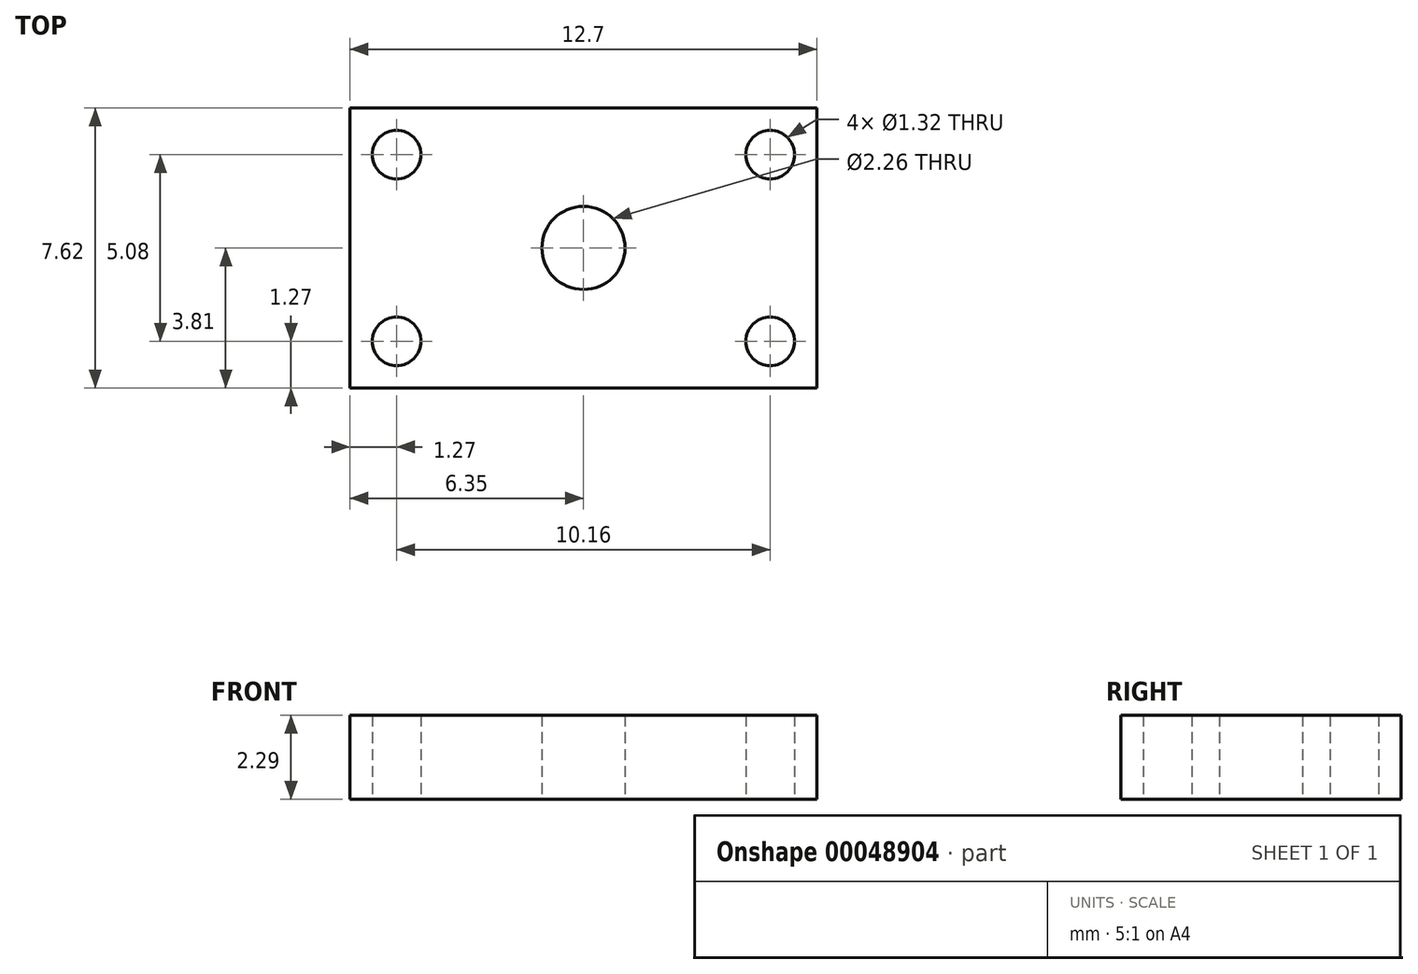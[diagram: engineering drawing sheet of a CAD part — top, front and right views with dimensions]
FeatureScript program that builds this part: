
annotation { "Feature Type Name" : "Feature", "Feature Type Description" : "" }
export const myFeature = defineFeature(function(context is Context, id is Id, definition is map)
    precondition{}
    {
        {
            var Q0;
            Q0=qCreatedBy(makeId("Top.planeOp"),FACE);
            var sketch = newSketch(context, id + "F0", { "sketchPlane" : qUnion([Q0])});
            skLineSegment(sketch, "E0.rect.bottom", {"start": v(-6.35, -3.8) * mm, "end": v(6.35, -3.8) * mm});
            skLineSegment(sketch, "E0.rect.top", {"start": v(-6.35, 3.8) * mm, "end": v(6.35, 3.8) * mm});
            skLineSegment(sketch, "E0.rect.left", {"start": v(-6.35, -3.8) * mm, "end": v(-6.35, 3.8) * mm});
            skLineSegment(sketch, "E0.rect.right", {"start": v(6.35, -3.8) * mm, "end": v(6.35, 3.8) * mm});
            skPoint(sketch, "E0.rect.middle", {"position": v(0, 0) * mm});
            skLineSegment(sketch, "E1.rect.bottom", {"start": v(-5.08, -2.54) * mm, "end": v(5.08, -2.54) * mm});
            skLineSegment(sketch, "E1.rect.top", {"start": v(-5.08, 2.54) * mm, "end": v(5.08, 2.54) * mm});
            skLineSegment(sketch, "E1.rect.left", {"start": v(-5.08, -2.54) * mm, "end": v(-5.08, 2.54) * mm});
            skLineSegment(sketch, "E1.rect.right", {"start": v(5.08, -2.54) * mm, "end": v(5.08, 2.54) * mm});
            skSolve(sketch);
        }
        {
            var Q0;
            Q0=makeQuery(id+"F0.imprint","IMPRINT",FACE,{"disambiguationData":[TD([[makeQuery(id+"F0.imprint","IMPRINT",EDGE,{"derivedFrom":sQuery(id+"F0.wireOp",EDGE,"E1.rect.bottom")}),1.0]])]});
            var Q1;
            Q1=makeQuery(id+"F0.imprint","IMPRINT",FACE,{"disambiguationData":[TD([[makeQuery(id+"F0.imprint","IMPRINT",EDGE,{"derivedFrom":sQuery(id+"F0.wireOp",EDGE,"E0.rect.bottom")}),1.0]])]});
            extrude(context, id + "F1", {"entities" : qUnion([Q0, Q1]), "depth" : 2.3 * mm});
        }
        {
            var Q0;
            Q0=sQuery(id+"F0.wireOp",VERTEX,"E1.rect.left.end");
            var Q1;
            Q1=sQuery(id+"F0.wireOp",VERTEX,"E1.rect.right.end");
            var Q2;
            Q2=sQuery(id+"F0.wireOp",VERTEX,"E1.rect.right.start");
            var Q3;
            Q3=sQuery(id+"F0.wireOp",VERTEX,"E1.rect.left.start");
            var Q4;
            Q4=makeQuery(id+"F1.opExtrude","SWEPT_BODY",BODY,{"disambiguationData":[OSD([sQuery(id+"F0.wireOp",EDGE,"E0.rect.bottom"),sQuery(id+"F0.wireOp",EDGE,"E0.rect.top"),sQuery(id+"F0.wireOp",EDGE,"E0.rect.left"),sQuery(id+"F0.wireOp",EDGE,"E0.rect.right")])]});
            hole(context, id + "F2", {"style" : HoleStyle.SIMPLE, "holeDiameter" : 1.32 * mm, "endStyle" : HoleEndStyle.THROUGH, "oppositeDirection" : true, "locations" : qUnion([Q0, Q1, Q2, Q3]), "scope" : qUnion([Q4])});
        }
        {
            var Q0;
            Q0=sQuery(id+"F0.wireOp",VERTEX,"E0.rect.middle");
            var Q1;
            Q1=makeQuery(id+"F1.opExtrude","SWEPT_BODY",BODY,{"disambiguationData":[OSD([sQuery(id+"F0.wireOp",EDGE,"E0.rect.bottom"),sQuery(id+"F0.wireOp",EDGE,"E0.rect.top"),sQuery(id+"F0.wireOp",EDGE,"E0.rect.left"),sQuery(id+"F0.wireOp",EDGE,"E0.rect.right")])]});
            hole(context, id + "F3", {"style" : HoleStyle.SIMPLE, "holeDiameter" : 2.26 * mm, "endStyle" : HoleEndStyle.THROUGH, "oppositeDirection" : true, "locations" : qUnion([Q0]), "scope" : qUnion([Q1])});
        }
    });
